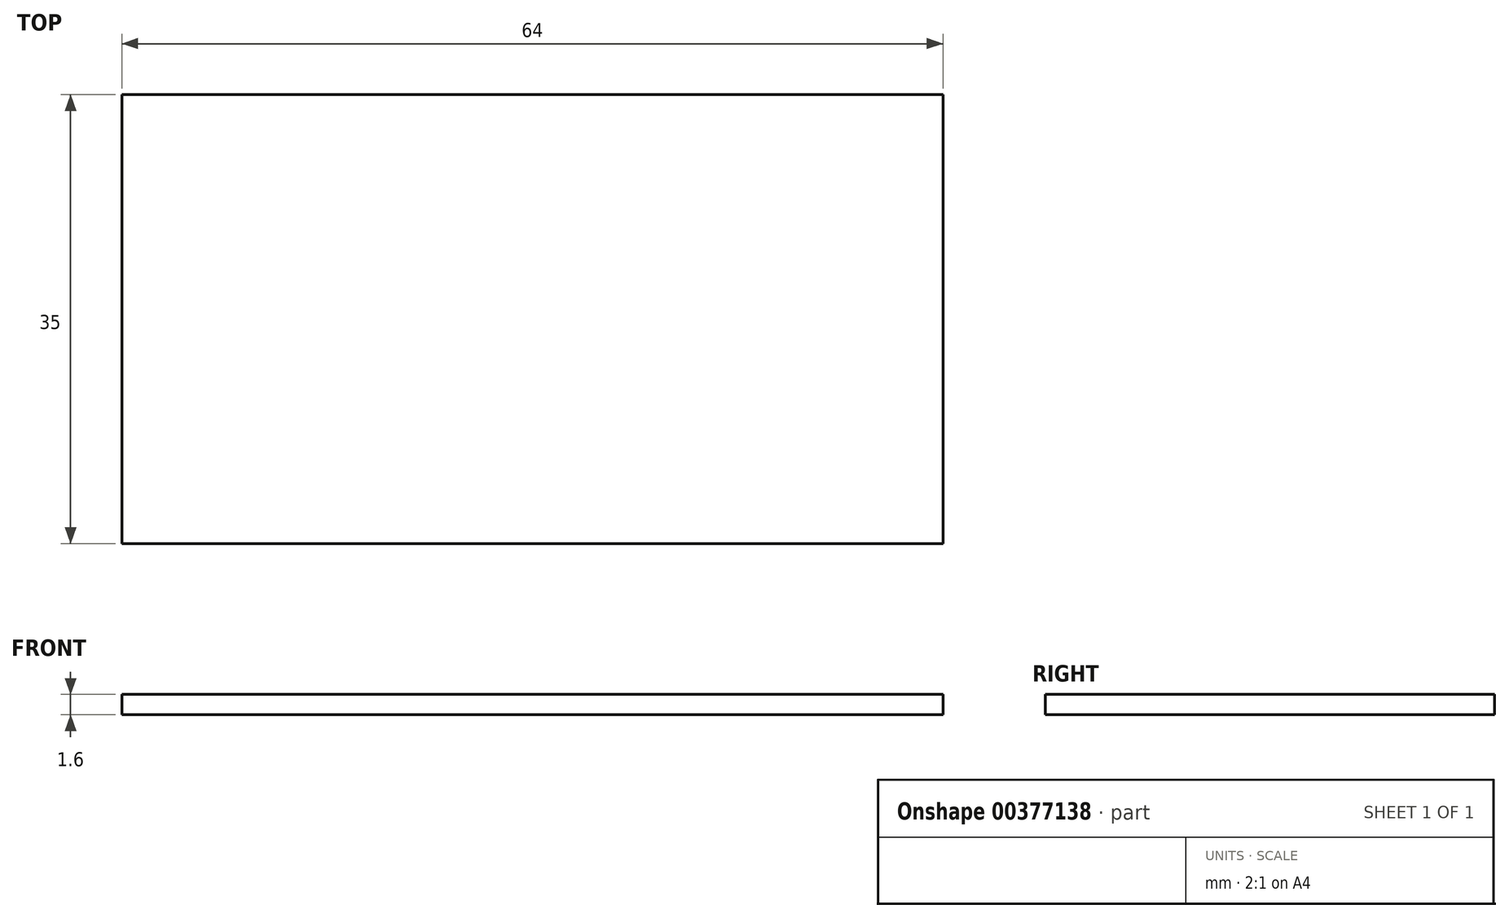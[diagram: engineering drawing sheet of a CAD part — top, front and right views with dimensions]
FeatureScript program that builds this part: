
annotation { "Feature Type Name" : "Feature", "Feature Type Description" : "" }
export const myFeature = defineFeature(function(context is Context, id is Id, definition is map)
    precondition{}
    {
        {
            var Q0;
            Q0=qCreatedBy(makeId("Top.planeOp"),FACE);
            var sketch = newSketch(context, id + "F0", { "sketchPlane" : qUnion([Q0])});
            skLineSegment(sketch, "E0.bottom", {"start": v(-32, 17.5) * mm, "end": v(32, 17.5) * mm});
            skLineSegment(sketch, "E0.top", {"start": v(-32, -17.5) * mm, "end": v(32, -17.5) * mm});
            skLineSegment(sketch, "E0.left", {"start": v(-32, 17.5) * mm, "end": v(-32, -17.5) * mm});
            skLineSegment(sketch, "E0.right", {"start": v(32, 17.5) * mm, "end": v(32, -17.5) * mm});
            skPoint(sketch, "E0.middle", {"position": v(0, 0) * mm});
            skSolve(sketch);
        }
        {
            var Q0;
            Q0 = qSketchRegion(id + "F0", true);
            extrude(context, id + "F1", {"entities" : qUnion([Q0]), "depth" : 1.6 * mm});
        }
    });
